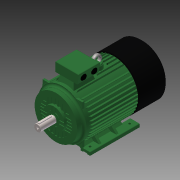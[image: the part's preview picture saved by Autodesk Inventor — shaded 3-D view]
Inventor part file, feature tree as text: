
AUTODESK INVENTOR PART (.ipt)
format: ipt  version: 2015 SP1 (Build 190203100, 203)  size: 1,069,568 bytes
history: native  units: in
note: dims shown in document units (in); Inventor stores cm internally (conversion verified against a paired STEP export)
features: other x4, fillet x1
ambient origin geometry x8: Origin, YZ Plane, XZ Plane, XY Plane, X Axis, Y Axis, Z Axis, Center Point
bodies: Solid1 (feature_tree), Solid2 (feature_tree), Solid3 (feature_tree)
feature tree (5):
  other  "TMDF 180L.ipt"
  other  "Cut-Extrude3[1]::TMDF 180L.ipt"
  other  "Cut-Extrude3[2]::TMDF 180L.ipt"
  fillet  "Fillet3::TMDF 180L.ipt"  Radius=0.1772in
  other  "TaggingFeature1"
